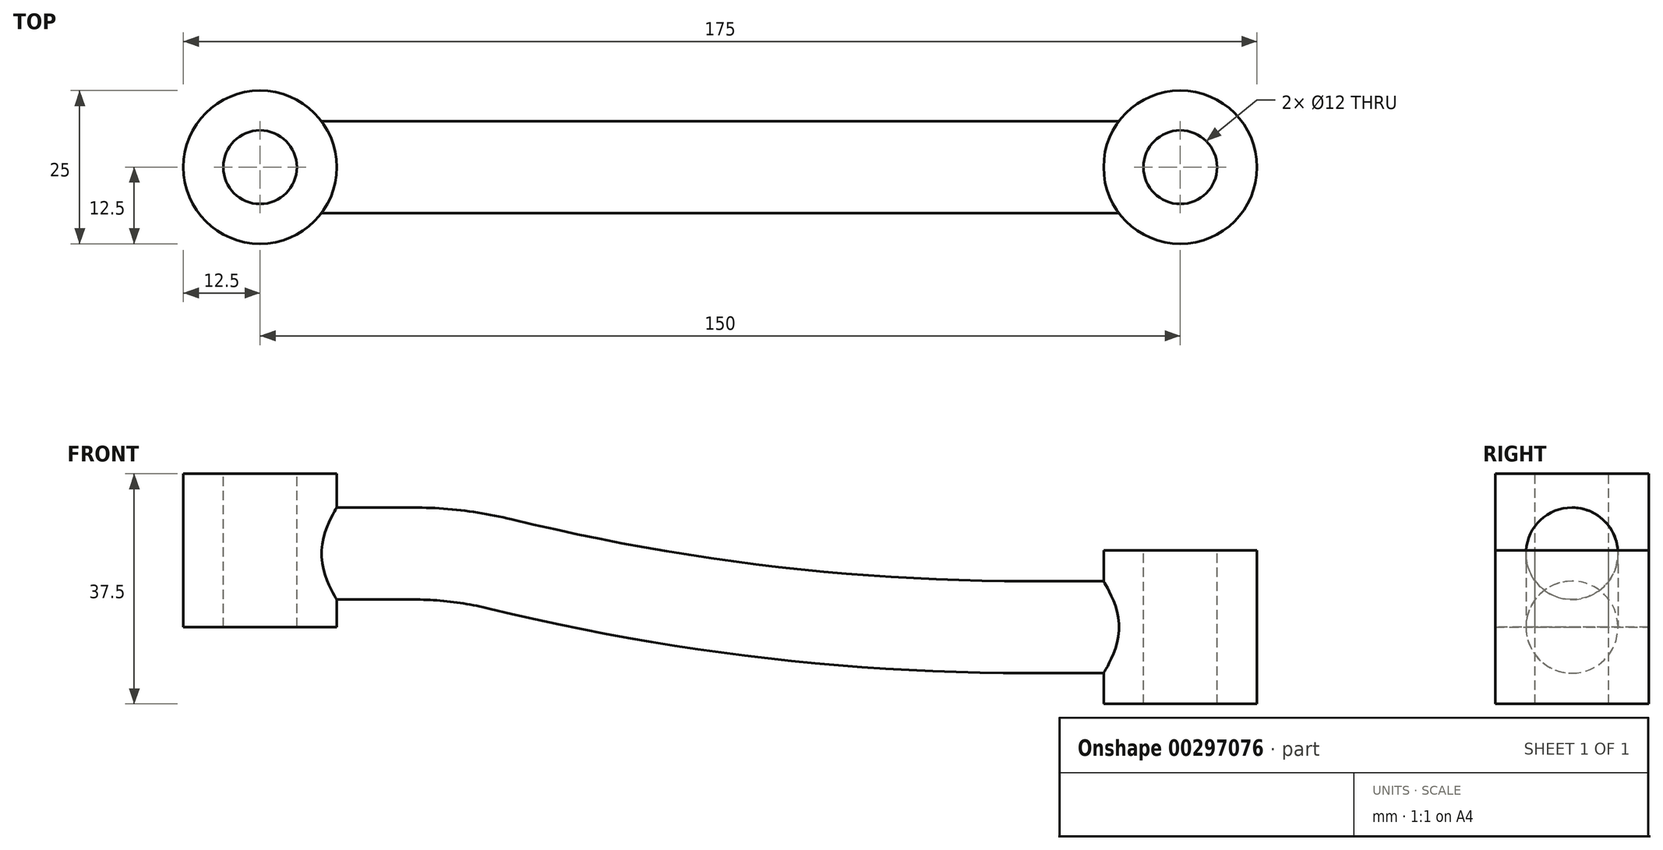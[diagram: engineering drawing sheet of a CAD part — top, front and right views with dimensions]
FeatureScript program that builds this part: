
annotation { "Feature Type Name" : "Feature", "Feature Type Description" : "" }
export const myFeature = defineFeature(function(context is Context, id is Id, definition is map)
    precondition{}
    {
        {
            var Q0;
            Q0=qCreatedBy(makeId("Top.planeOp"),FACE);
            var sketch = newSketch(context, id + "F0", { "sketchPlane" : qUnion([Q0])});
            skCircle(sketch, "E0", {"center": v(0, 0) * mm, "radius": 12.5 * mm});
            skCircle(sketch, "E1", {"center": v(150, 0) * mm, "radius": 12.5 * mm});
            skSolve(sketch);
        }
        {
            var Q0;
            Q0=makeQuery(id+"F0.imprint","IMPRINT",FACE,{"disambiguationData":[TD([[makeQuery(id+"F0.imprint","IMPRINT",EDGE,{"derivedFrom":sQuery(id+"F0.wireOp",EDGE,"E0")}),1.0]])]});
            extrude(context, id + "F1", {"entities" : qUnion([Q0]), "depth" : 25 * mm});
        }
        {
            var Q0;
            Q0=makeQuery(id+"F0.imprint","IMPRINT",FACE,{"disambiguationData":[TD([[makeQuery(id+"F0.imprint","IMPRINT",EDGE,{"derivedFrom":sQuery(id+"F0.wireOp",EDGE,"E1")}),1.0]])]});
            extrude(context, id + "F2", {"entities" : qUnion([Q0]), "endBound" : BoundingType.SYMMETRIC, "depth" : 25 * mm});
        }
        {
            var Q0;
            Q0=qCreatedBy(makeId("Front.planeOp"),FACE);
            var sketch = newSketch(context, id + "F3", { "sketchPlane" : qUnion([Q0])});
            skLineSegment(sketch, "E2", {"start": v(0, 12) * mm, "end": v(25, 12) * mm});
            skArc(sketch, "E3", {"start": v(39.2, 10.3) * mm, "mid": v(32.15, 11.57) * mm, "end": v(25, 12) * mm});
            skArc(sketch, "E4", {"start": v(39.2, 10.3) * mm, "mid": v(81.79, 2.58) * mm, "end": v(125, 0) * mm});
            skLineSegment(sketch, "E5", {"start": v(125, 0) * mm, "end": v(150, 0) * mm});
            skSolve(sketch);
        }
        {
            var Q0;
            Q0=qCreatedBy(makeId("Right.planeOp"),FACE);
            var sketch = newSketch(context, id + "F4", { "sketchPlane" : qUnion([Q0])});
            skCircle(sketch, "E6", {"center": v(0, 12) * mm, "radius": 7.5 * mm});
            skSolve(sketch);
        }
        {
            var Q0;
            Q0 = qSketchRegion(id + "F4", true);
            var Q1;
            Q1 = qConstructionFilter(qBodyType(qCreatedBy(id + "F3" ,EDGE), BodyType.WIRE), ConstructionObject.NO);
            sweep(context, id + "F5", {"operationType" : NewBodyOperationType.ADD, "profiles" : qUnion([Q0]), "path" : qUnion([Q1])});
        }
        {
            var Q0;
            Q0=makeQuery(id+"F1.opExtrude","CAP_FACE",FACE,{"disambiguationData":[OSD([sQuery(id+"F0.wireOp",EDGE,"E0")])],"isStart":false});
            var sketch = newSketch(context, id + "F6", { "sketchPlane" : qUnion([Q0])});
            skCircle(sketch, "E7", {"center": v(0, 0) * mm, "radius": 6 * mm});
            skCircle(sketch, "E8", {"center": v(150, 0) * mm, "radius": 6 * mm});
            skSolve(sketch);
        }
        {
            var Q0;
            Q0 = qSketchRegion(id + "F6", true);
            extrude(context, id + "F7", {"entities" : qUnion([Q0]), "operationType" : NewBodyOperationType.REMOVE, "endBound" : BoundingType.THROUGH_ALL, "oppositeDirection" : true, "depth" : mm});
        }
    });
